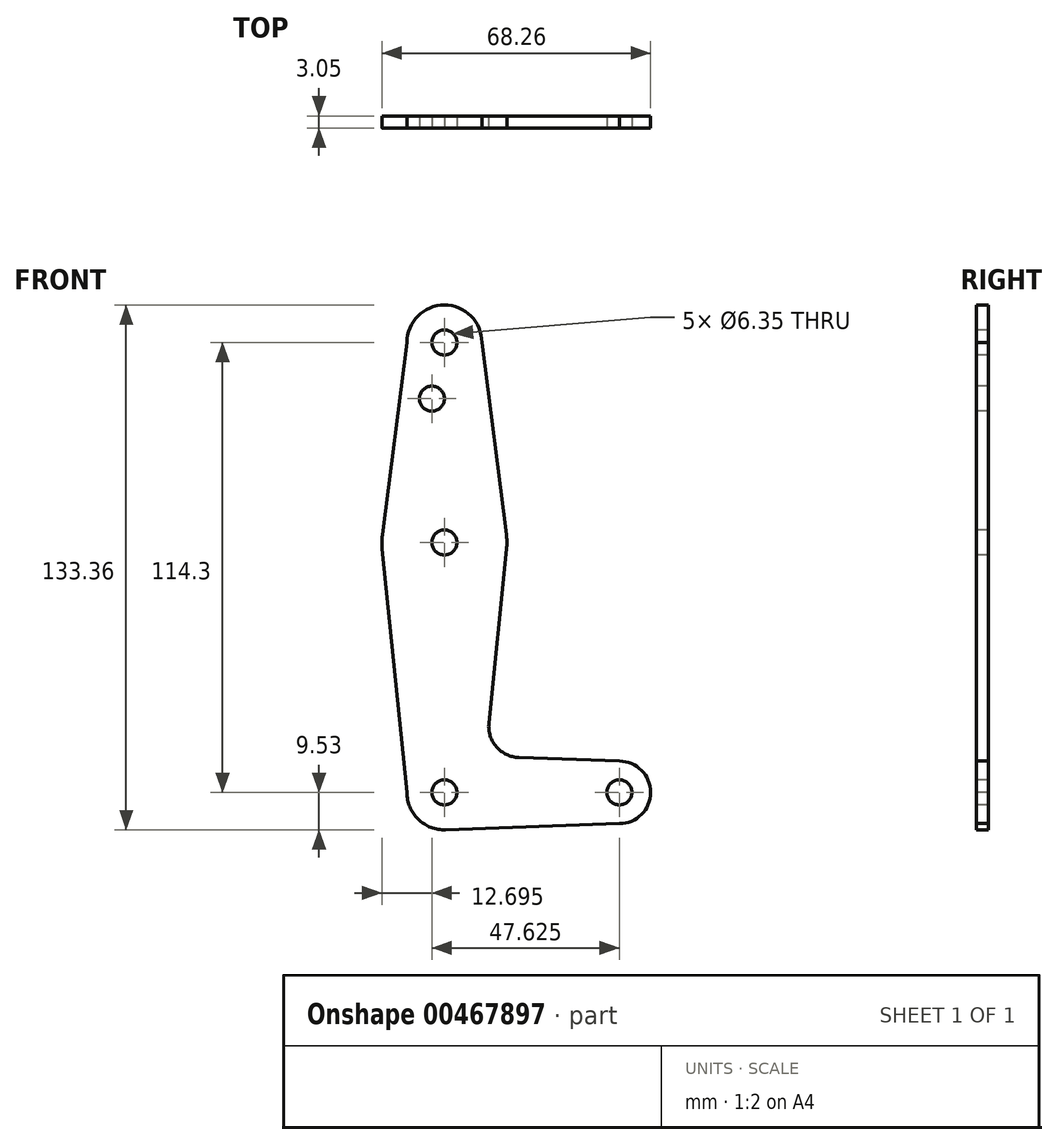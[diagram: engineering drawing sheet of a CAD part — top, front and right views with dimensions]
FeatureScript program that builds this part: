
annotation { "Feature Type Name" : "Feature", "Feature Type Description" : "" }
export const myFeature = defineFeature(function(context is Context, id is Id, definition is map)
    precondition{}
    {
        {
            var Q0;
            Q0=qCreatedBy(makeId("Front.planeOp"),FACE);
            var sketch = newSketch(context, id + "F0", { "sketchPlane" : qUnion([Q0])});
            skCircle(sketch, "E0", {"center": v(0, 114.3) * mm, "radius": 9.53 * mm});
            skCircle(sketch, "E1", {"center": v(0, 63.5) * mm, "radius": 15.88 * mm});
            skCircle(sketch, "E2", {"center": v(0, 0) * mm, "radius": 9.53 * mm});
            skCircle(sketch, "E3", {"center": v(44.45, 0) * mm, "radius": 7.94 * mm});
            skLineSegment(sketch, "E4", {"start": v(0, 63.5) * mm, "end": v(0, 0) * mm, "construction": true});
            skLineSegment(sketch, "E5", {"start": v(0, 0) * mm, "end": v(44.45, 0) * mm, "construction": true});
            skLineSegment(sketch, "E6", {"start": v(0, 63.5) * mm, "end": v(0, 114.3) * mm, "construction": true});
            skLineSegment(sketch, "E7", {"start": v(9.53, 114.3) * mm, "end": v(15.75, 65.5) * mm});
            skLineSegment(sketch, "E8", {"start": v(-9.53, 114.3) * mm, "end": v(-15.75, 65.5) * mm});
            skLineSegment(sketch, "E9", {"start": v(-9.53, 0) * mm, "end": v(-15.8, 61.9) * mm});
            skLineSegment(sketch, "E10", {"start": v(11.3, 17.6) * mm, "end": v(15.8, 61.9) * mm});
            skLineSegment(sketch, "E11", {"start": v(44.45, 7.94) * mm, "end": v(18.93, 8.85) * mm});
            skLineSegment(sketch, "E12", {"start": v(44.45, -7.94) * mm, "end": v(0.34, -9.52) * mm});
            skPoint(sketch, "E13.newPointB", {"position": v(9.53, 0) * mm});
            skArc(sketch, "E13.filletArc", {"start": v(11.3, 17.6) * mm, "mid": v(13.22, 11.57) * mm, "end": v(18.93, 8.85) * mm});
            skCircle(sketch, "E14", {"center": v(0, 114.3) * mm, "radius": 3.18 * mm});
            skCircle(sketch, "E15", {"center": v(0, 63.5) * mm, "radius": 3.18 * mm});
            skCircle(sketch, "E16", {"center": v(-3.17, 100.03) * mm, "radius": 3.18 * mm});
            skCircle(sketch, "E17", {"center": v(0, 0) * mm, "radius": 3.18 * mm});
            skCircle(sketch, "E18", {"center": v(44.45, 0) * mm, "radius": 3.18 * mm});
            skSolve(sketch);
        }
        {
            var Q0;
            Q0 = qSketchRegion(id + "F0", true);
            extrude(context, id + "F1", {"entities" : qUnion([Q0]), "oppositeDirection" : true, "depth" : 3.05 * mm});
        }
    });
